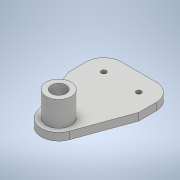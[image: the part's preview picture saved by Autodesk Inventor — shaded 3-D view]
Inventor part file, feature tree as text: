
AUTODESK INVENTOR PART (.ipt)
format: ipt  version: 2020 (Build 240168000, 168)  size: 140,800 bytes
history: native  units: mm
features: sketch x3, extrude x2, other x1, fillet x1, hole x1
ambient origin geometry x8: Origin, YZ Plane, XZ Plane, XY Plane, X Axis, Y Axis, Z Axis, Center Point
bodies: Body1 (feature_tree)
feature tree (8):
  other  "Твердое тело1"
  extrude  "Выдавливание1"  Depth=14.0mm
  extrude  "Выдавливание11"  Depth=7.0mm
  fillet  "Сопряжение1"  Radius=9.0mm
  hole  "Отверстие1"  [1 undecoded]
  sketch  "Эскиз1"
  sketch  "Эскиз2"
  sketch  "Эскиз5"
note: 1 required parameter value undecoded (feature->parameter linkage not recoverable at this tier; creation-order binding heuristic only, values carry confidence <= 0.55)
